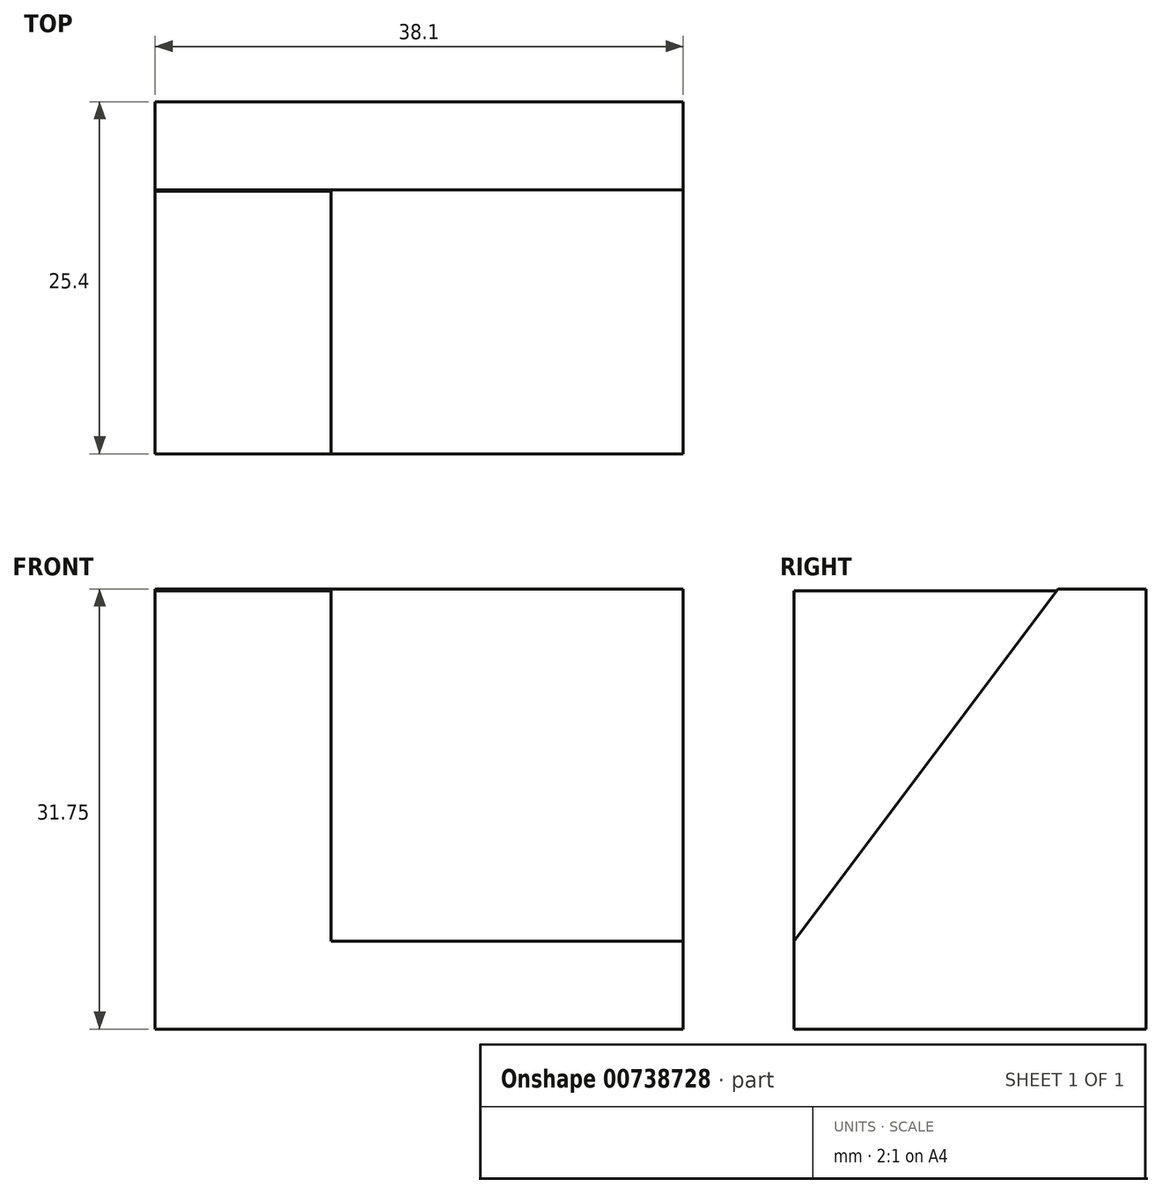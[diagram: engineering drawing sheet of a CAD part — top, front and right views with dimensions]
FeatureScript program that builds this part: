
annotation { "Feature Type Name" : "Feature", "Feature Type Description" : "" }
export const myFeature = defineFeature(function(context is Context, id is Id, definition is map)
    precondition{}
    {
        {
            var Q0;
            Q0=qCreatedBy(makeId("Right.planeOp"),FACE);
            var sketch = newSketch(context, id + "F0", { "sketchPlane" : qUnion([Q0])});
            skLineSegment(sketch, "E0", {"start": v(0, 0) * mm, "end": v(25.4, 0) * mm});
            skLineSegment(sketch, "E1", {"start": v(25.4, 0) * mm, "end": v(25.4, 31.75) * mm});
            skLineSegment(sketch, "E2", {"start": v(25.4, 31.75) * mm, "end": v(19.05, 31.75) * mm});
            skLineSegment(sketch, "E3", {"start": v(19.05, 31.75) * mm, "end": v(0, 6.35) * mm});
            skLineSegment(sketch, "E4", {"start": v(0, 6.35) * mm, "end": v(0, 0) * mm});
            skSolve(sketch);
        }
        {
            var Q0;
            Q0 = qSketchRegion(id + "F0", true);
            extrude(context, id + "F1", {"entities" : qUnion([Q0]), "depth" : 38.1 * mm, "offsetDistance" : 25.4 * mm});
        }
        {
            var Q0;
            Q0=qCreatedBy(makeId("Right.planeOp"),FACE);
            var sketch = newSketch(context, id + "F2", { "sketchPlane" : qUnion([Q0])});
            skLineSegment(sketch, "E5", {"start": v(19.05, 31.62) * mm, "end": v(0, 31.62) * mm});
            skLineSegment(sketch, "E6", {"start": v(0, 31.62) * mm, "end": v(0, 6.22) * mm});
            skLineSegment(sketch, "E7", {"start": v(0, 6.22) * mm, "end": v(19.05, 31.62) * mm});
            skSolve(sketch);
        }
        {
            var Q0;
            Q0 = qSketchRegion(id + "F2", true);
            extrude(context, id + "F3", {"entities" : qUnion([Q0]), "operationType" : NewBodyOperationType.ADD, "depth" : 12.7 * mm, "offsetDistance" : 25.4 * mm});
        }
    });
